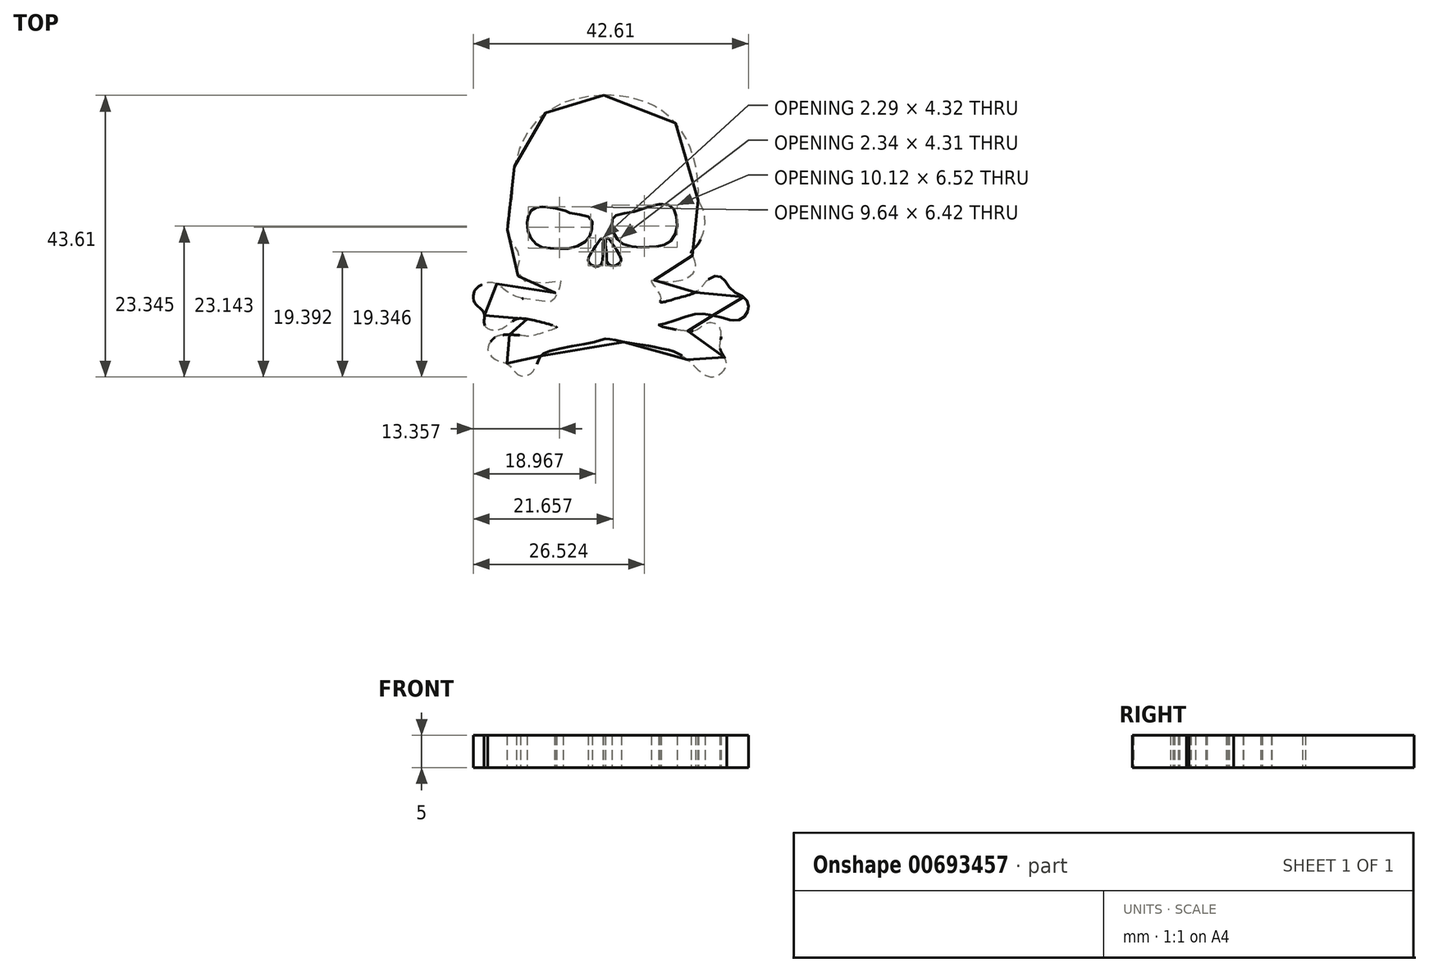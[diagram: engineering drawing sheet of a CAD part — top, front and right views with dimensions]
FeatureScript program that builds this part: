
annotation { "Feature Type Name" : "Feature", "Feature Type Description" : "" }
export const myFeature = defineFeature(function(context is Context, id is Id, definition is map)
    precondition{}
    {
        {
            var Q0;
            Q0=qCreatedBy(makeId("Top.planeOp"),FACE);
            var sketch = newSketch(context, id + "F0", { "sketchPlane" : qUnion([Q0])});
            skLineSegment(sketch, "E0.bottom", {"start": v(-23.86, 34.73) * mm, "end": v(26.14, 34.73) * mm});
            skLineSegment(sketch, "E0.top", {"start": v(-23.86, -19.85) * mm, "end": v(26.14, -19.85) * mm});
            skLineSegment(sketch, "E0.left", {"start": v(-23.86, 34.73) * mm, "end": v(-23.86, -19.85) * mm});
            skLineSegment(sketch, "E0.right", {"start": v(26.14, 34.73) * mm, "end": v(26.14, -19.85) * mm});
            skFitSpline(sketch, "E1", {"points": [v(-0.26, 7.14) * mm, v(-0.44, 7) * mm, v(-0.92, 6.33) * mm, v(-1.7, 5.14) * mm, v(-2.25, 4.2) * mm, v(-2.32, 3.45) * mm, v(-1.72, 2.85) * mm, v(-0.57, 2.82) * mm, v(-0.18, 3.48) * mm, v(-0.07, 5.24) * mm, v(-0.07, 6.56) * mm, v(-0.09, 6.92) * mm, v(-0.26, 7.14) * mm]});
            skFitSpline(sketch, "E2", {"points": [v(0.55, 7.1) * mm, v(0.36, 6.85) * mm, v(0.36, 5.42) * mm, v(0.5, 4.06) * mm, v(0.68, 3.05) * mm, v(1.69, 2.8) * mm, v(2.52, 3.26) * mm, v(2.72, 3.77) * mm, v(0.8, 6.95) * mm, v(0.55, 7.1) * mm]});
            skFitSpline(sketch, "E3", {"points": [v(10.15, 12.2) * mm, v(9, 12.34) * mm, v(8.72, 12.34) * mm, v(7.02, 11.97) * mm, v(4.61, 11.15) * mm, v(2.1, 10.67) * mm, v(1.39, 10.05) * mm, v(1.35, 8.66) * mm, v(1.91, 7.23) * mm, v(3.16, 6.11) * mm, v(5.67, 5.68) * mm, v(7.67, 5.73) * mm, v(9.27, 6.02) * mm, v(10.7, 6.98) * mm, v(11.4, 9.11) * mm, v(11, 11.27) * mm, v(10.15, 12.2) * mm]});
            skFitSpline(sketch, "E4", {"points": [v(-9.5, 11.94) * mm, v(-10.37, 11.86) * mm, v(-11.08, 11.5) * mm, v(-11.62, 10.65) * mm, v(-11.8, 9.75) * mm, v(-11.74, 8.33) * mm, v(-11.27, 7.05) * mm, v(-10.18, 5.96) * mm, v(-9.11, 5.56) * mm, v(-7.37, 5.48) * mm, v(-5.56, 5.47) * mm, v(-3.5, 6.04) * mm, v(-2.39, 7.06) * mm, v(-1.9, 8.15) * mm, v(-1.75, 9.46) * mm, v(-2.13, 10.28) * mm, v(-3.66, 10.72) * mm, v(-5.5, 11.09) * mm, v(-5.66, 11.2) * mm, v(-7.65, 11.72) * mm, v(-9.02, 11.91) * mm, v(-9.5, 11.94) * mm]});
            skFitSpline(sketch, "E5", {"points": [v(0, 29.2) * mm, v(-1.16, 29.15) * mm, v(-3.14, 28.9) * mm, v(-5.32, 28.36) * mm, v(-6.31, 28.01) * mm, v(-8.65, 26.7) * mm, v(-9.98, 25.63) * mm, v(-11.08, 24.52) * mm, v(-12.65, 21.87) * mm, v(-13.18, 20.49) * mm, v(-13.74, 18.38) * mm, v(-14.07, 16.64) * mm, v(-14.18, 12.82) * mm, v(-14.28, 12.45) * mm, v(-14.67, 11.79) * mm, v(-14.98, 9.52) * mm, v(-14.68, 7.47) * mm, v(-13.89, 5.64) * mm, v(-13.05, 4.77) * mm, v(-12.89, 4.23) * mm, v(-13.34, 2.98) * mm, v(-13.5, 2.22) * mm, v(-13.1, 1.06) * mm, v(-11.27, 0.22) * mm, v(-7.75, 0.3) * mm, v(-6.44, 0.45) * mm, v(-6.28, 0.3) * mm, v(-7, -0.83) * mm, v(-7.62, -1.84) * mm, v(-7.47, -3.02) * mm, v(-7.97, -2.92) * mm, v(-13.4, -2.03) * mm, v(-15.94, -0.4) * mm, v(-17.21, 0.19) * mm, v(-18.58, 0) * mm, v(-19.55, -0.57) * mm, v(-20.09, -1.42) * mm, v(-19.93, -3) * mm, v(-18.61, -4.34) * mm, v(-18.49, -5.93) * mm, v(-18.23, -6.67) * mm, v(-17.22, -7.14) * mm, v(-15.62, -6.83) * mm, v(-13.9, -5.65) * mm, v(-11.95, -5.43) * mm, v(-7.26, -6.72) * mm, v(-7.43, -6.9) * mm, v(-11.02, -8.05) * mm, v(-12.01, -8.09) * mm, v(-16, -7.98) * mm, v(-17.35, -8.8) * mm, v(-17.84, -9.66) * mm, v(-17.73, -10.82) * mm, v(-15.98, -12.06) * mm, v(-15.41, -12.17) * mm, v(-14.85, -12.4) * mm, v(-13.86, -13.5) * mm, v(-12.83, -14.24) * mm, v(-11.96, -14.18) * mm, v(-11.16, -13.8) * mm, v(-10.27, -12.28) * mm, v(-9.85, -11.38) * mm, v(-8.75, -10.54) * mm, v(-1.33, -8.97) * mm, v(0.42, -8.5) * mm, v(2.25, -8.82) * mm, v(5.52, -9.39) * mm, v(7.52, -9.71) * mm, v(10.35, -10.34) * mm, v(11.62, -10.85) * mm, v(13, -11.71) * mm, v(14.6, -13.27) * mm, v(16.18, -14.31) * mm, v(17.49, -14.27) * mm, v(18.7, -13.29) * mm, v(19, -12.05) * mm, v(18.06, -10.05) * mm, v(18.22, -7.83) * mm, v(17.33, -6.18) * mm, v(15.37, -6.41) * mm, v(14.01, -7.27) * mm, v(8.52, -6.44) * mm, v(9.08, -6.27) * mm, v(13.21, -4.94) * mm, v(15.99, -4.72) * mm, v(19.4, -5.52) * mm, v(19.91, -5.64) * mm, v(21.16, -5.57) * mm, v(22.2, -4.49) * mm, v(22.43, -3.35) * mm, v(21.9, -2.2) * mm, v(19.88, -0.98) * mm, v(18.65, 0.67) * mm, v(17.46, 1.23) * mm, v(15.77, 0.25) * mm, v(14.57, -1.11) * mm, v(11.14, -2.3) * mm, v(8.8, -2.86) * mm, v(8.82, -2.57) * mm, v(8.76, -1.66) * mm, v(7.39, 0.47) * mm, v(8.44, 0.45) * mm, v(11.02, 0.4) * mm, v(13, 0.96) * mm, v(14.13, 2.1) * mm, v(14.24, 3.08) * mm, v(13.8, 4.31) * mm, v(13.58, 4.78) * mm, v(13.6, 5.03) * mm, v(14.52, 6.02) * mm, v(15.4, 7.82) * mm, v(15.56, 11.15) * mm, v(14.62, 13.02) * mm, v(14.65, 13.44) * mm, v(14.5, 16.82) * mm, v(13.3, 21.42) * mm, v(11.45, 24.52) * mm, v(8.78, 27) * mm, v(6.02, 28.32) * mm, v(2.83, 29.06) * mm, v(0, 29.2) * mm]});
            skSolve(sketch);
        }
        {
            var Q0;
            Q0=sQuery(id+"F0.wireOp",EDGE,"E3");
            var Q1;
            Q1=sQuery(id+"F0.wireOp",EDGE,"E4");
            var Q2;
            Q2=sQuery(id+"F0.wireOp",EDGE,"E5");
            var Q3;
            Q3=sQuery(id+"F0.wireOp",EDGE,"E2");
            var Q4;
            Q4=sQuery(id+"F0.wireOp",EDGE,"E1");
            extrude(context, id + "F1", {"bodyType" : ToolBodyType.SURFACE, "surfaceEntities" : qUnion([Q0, Q1, Q2, Q3, Q4]), "depth" : 5 * mm, "offsetDistance" : 25 * mm});
        }
        {
            var Q0;
            Q0=makeQuery(id+"F0.imprint","IMPRINT",FACE,{"disambiguationData":[TD([[makeQuery(id+"F0.imprint","IMPRINT",EDGE,{"derivedFrom":sQuery(id+"F0.wireOp",EDGE,"E1")}),-1.0]])]});
            extrude(context, id + "F2", {"entities" : qUnion([Q0]), "depth" : 5 * mm, "offsetDistance" : 25 * mm});
        }
    });
